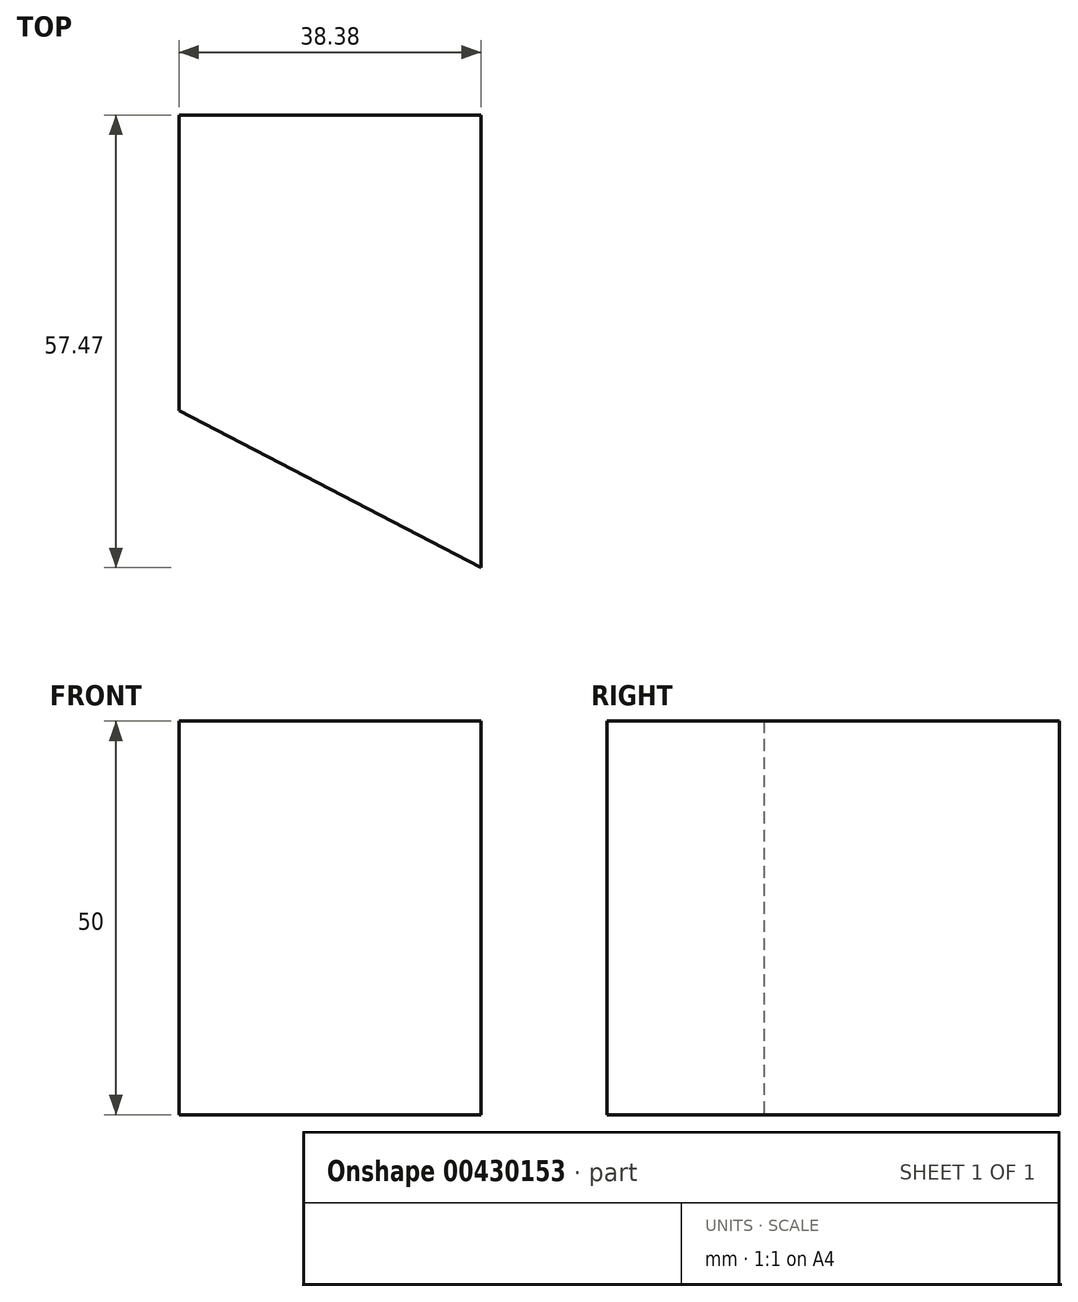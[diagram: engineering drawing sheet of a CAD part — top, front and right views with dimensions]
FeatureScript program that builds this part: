
annotation { "Feature Type Name" : "Feature", "Feature Type Description" : "" }
export const myFeature = defineFeature(function(context is Context, id is Id, definition is map)
    precondition{}
    {
        {
            var Q0;
            Q0=qCreatedBy(makeId("Top.planeOp"),FACE);
            var sketch = newSketch(context, id + "F0", { "sketchPlane" : qUnion([Q0])});
            skLineSegment(sketch, "E0", {"start": v(0, 57.47) * mm, "end": v(38.38, 57.47) * mm});
            skLineSegment(sketch, "E1", {"start": v(38.38, 57.47) * mm, "end": v(38.38, 0) * mm});
            skLineSegment(sketch, "E2", {"start": v(38.38, 0) * mm, "end": v(0, 19.92) * mm});
            skLineSegment(sketch, "E3", {"start": v(0, 19.92) * mm, "end": v(0, 68.46) * mm});
            skSolve(sketch);
        }
        {
            var Q0;
            {var subQ0=sQuery(id+"F0.wireOp",EDGE,"E0");Q0=makeQuery(id+"F0.imprint","IMPRINT",FACE,{"disambiguationData":[TD([[makeQuery(id+"F0.imprint","IMPRINT",EDGE,{"derivedFrom":subQ0}),-1.0]])]});}
            extrude(context, id + "F1", {"entities" : qUnion([Q0]), "depth" : 50 * mm});
        }
    });
